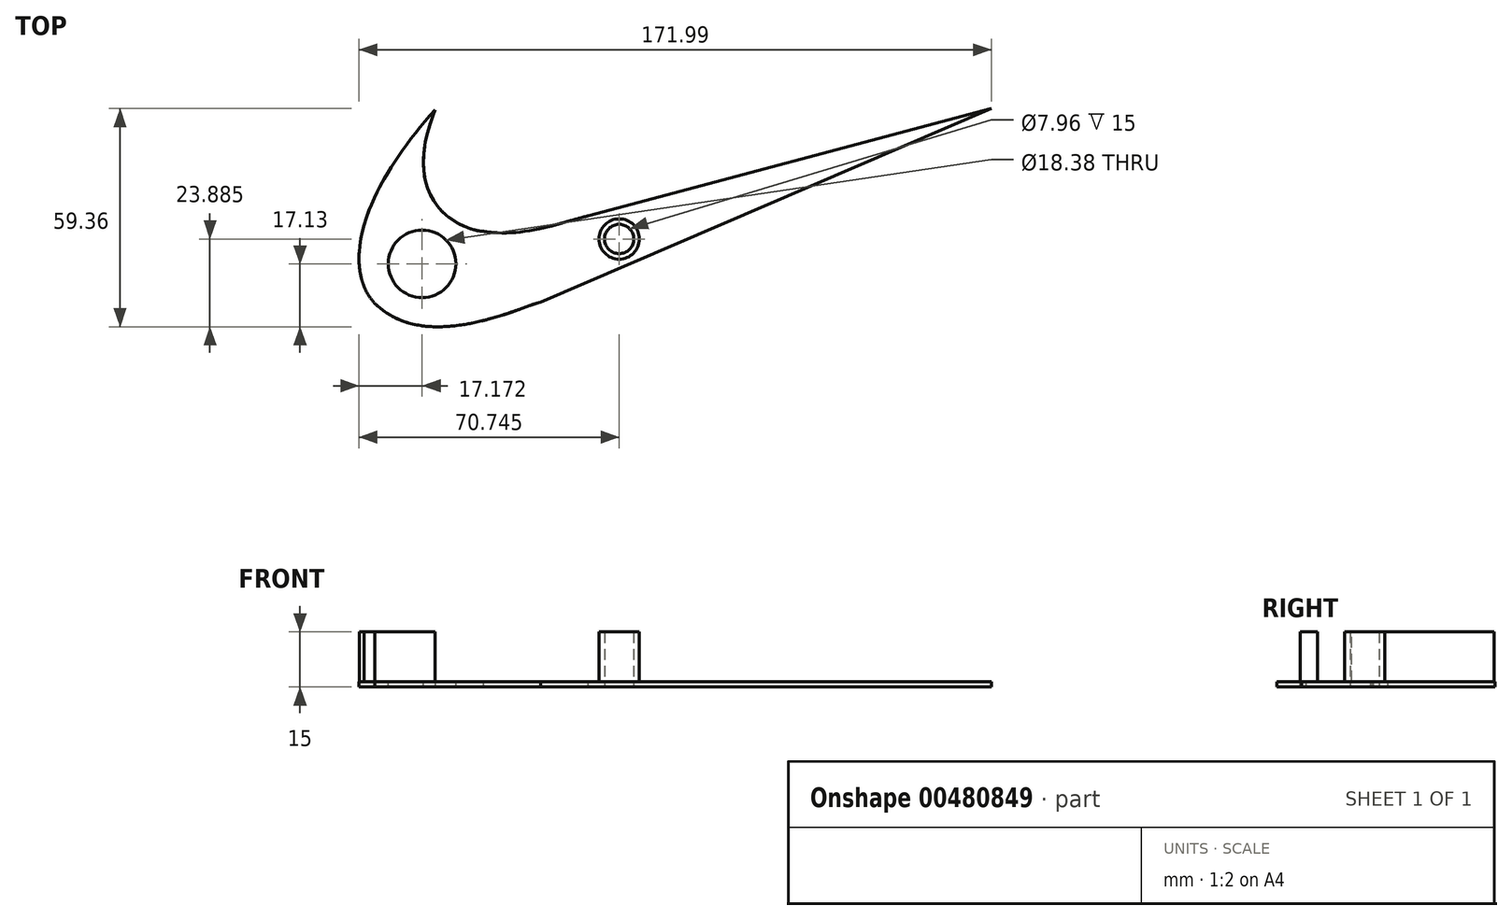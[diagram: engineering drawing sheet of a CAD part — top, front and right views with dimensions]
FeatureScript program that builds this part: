
annotation { "Feature Type Name" : "Feature", "Feature Type Description" : "" }
export const myFeature = defineFeature(function(context is Context, id is Id, definition is map)
    precondition{}
    {
        {
            var Q0;
            Q0=qCreatedBy(makeId("Top.planeOp"),FACE);
            var sketch = newSketch(context, id + "F0", { "sketchPlane" : qUnion([Q0])});
            skFitSpline(sketch, "E0", {"points": [v(-68.46, 37.52) * mm, v(-60.6, -2.11) * mm], "startDerivative": vector(-55.47, -100.99) * mm, "endDerivative": vector(10.44, -0.14) * mm});
            skFitSpline(sketch, "E1", {"points": [v(-60.6, -2.11) * mm, v(-32.66, 2.08) * mm], "startDerivative": vector(31.9, -4.9) * mm, "endDerivative": vector(25.54, 6.24) * mm});
            skFitSpline(sketch, "E2", {"points": [v(-32.66, 2.08) * mm, v(96.88, 36.55) * mm], "startDerivative": vector(129.54, 34.47) * mm, "endDerivative": vector(129.54, 34.47) * mm});
            skFitSpline(sketch, "E3", {"points": [v(96.88, 36.55) * mm, v(-44.73, -24.22) * mm], "startDerivative": vector(-141.62, -60.77) * mm, "endDerivative": vector(-141.62, -60.77) * mm});
            skFitSpline(sketch, "E4", {"points": [v(-44.73, -24.22) * mm, v(-91.41, -24.22) * mm], "startDerivative": vector(-25.05, -7.71) * mm, "endDerivative": vector(-42.25, 42.01) * mm});
            skFitSpline(sketch, "E5", {"points": [v(-91.41, -24.22) * mm, v(-68.46, 37.52) * mm], "startDerivative": vector(-27.32, 29.62) * mm, "endDerivative": vector(89.42, 90.17) * mm});
            skCircle(sketch, "E6", {"center": v(-77.47, -12.43) * mm, "radius": 7.7 * mm});
            skCircle(sketch, "E7", {"center": v(-23.9, -5.68) * mm, "radius": 3.98 * mm});
            skSolve(sketch);
        }
        {
            var Q0;
            Q0=makeQuery(id+"F0.imprint","IMPRINT",FACE,{"disambiguationData":[TD([[makeQuery(id+"F0.imprint","IMPRINT",EDGE,{"derivedFrom":sQuery(id+"F0.wireOp",EDGE,"E0")}),-1.0]])]});
            extrude(context, id + "F1", {"entities" : qUnion([Q0]), "depth" : 15 * mm});
        }
        {
            var Q0;
            Q0=makeQuery(id+"F1.opExtrude","CAP_FACE",FACE,{"disambiguationData":[OSD([sQuery(id+"F0.wireOp",EDGE,"E0"),sQuery(id+"F0.wireOp",EDGE,"E1"),sQuery(id+"F0.wireOp",EDGE,"E2"),sQuery(id+"F0.wireOp",EDGE,"E3"),sQuery(id+"F0.wireOp",EDGE,"E4"),sQuery(id+"F0.wireOp",EDGE,"E5")])],"isStart":false});
            shell(context, id + "F2", {"entities" : qUnion([Q0]), "thickness" : 1.5 * mm});
        }
        {
            var Q0;
            {var subQ0=sQuery(id+"F0.wireOp",EDGE,"E7");var subQ1=sQuery(id+"F0.wireOp",EDGE,"E6");var subQ2=sQuery(id+"F0.wireOp",EDGE,"E5");var subQ3=sQuery(id+"F0.wireOp",EDGE,"E4");var subQ4=sQuery(id+"F0.wireOp",EDGE,"E3");var subQ5=sQuery(id+"F0.wireOp",EDGE,"E2");var subQ6=sQuery(id+"F0.wireOp",EDGE,"E1");var subQ7=sQuery(id+"F0.wireOp",EDGE,"E0");Q0=makeQuery(id+"F2.opShell","OFFSET_FACE",FACE,{"disambiguationData":[OSD([subQ7,subQ6,subQ5,subQ4,subQ3,subQ2,subQ1,subQ0]),TDD([makeQuery(id+"F1.opExtrude","CAP_FACE",FACE,{"disambiguationData":[OSD([subQ7,subQ6,subQ5,subQ4,subQ3,subQ2,subQ1,subQ0])],"isStart":false})]),OD(0.0)]});}
            var Q1;
            {var subQ0=sQuery(id+"F0.wireOp",EDGE,"E7");var subQ1=sQuery(id+"F0.wireOp",EDGE,"E6");var subQ2=sQuery(id+"F0.wireOp",EDGE,"E5");var subQ3=sQuery(id+"F0.wireOp",EDGE,"E4");var subQ4=sQuery(id+"F0.wireOp",EDGE,"E3");var subQ5=sQuery(id+"F0.wireOp",EDGE,"E2");var subQ6=sQuery(id+"F0.wireOp",EDGE,"E1");var subQ7=sQuery(id+"F0.wireOp",EDGE,"E0");Q1=makeQuery(id+"F2.opShell","OFFSET_FACE",FACE,{"disambiguationData":[OSD([subQ7,subQ6,subQ5,subQ4,subQ3,subQ2,subQ1,subQ0]),TDD([makeQuery(id+"F1.opExtrude","CAP_FACE",FACE,{"disambiguationData":[OSD([subQ7,subQ6,subQ5,subQ4,subQ3,subQ2,subQ1,subQ0])],"isStart":false})]),OD(1.0)]});}
            extrude(context, id + "F3", {"entities" : qUnion([Q0, Q1]), "operationType" : NewBodyOperationType.REMOVE, "oppositeDirection" : true, "depth" : 25 * mm});
        }
    });
